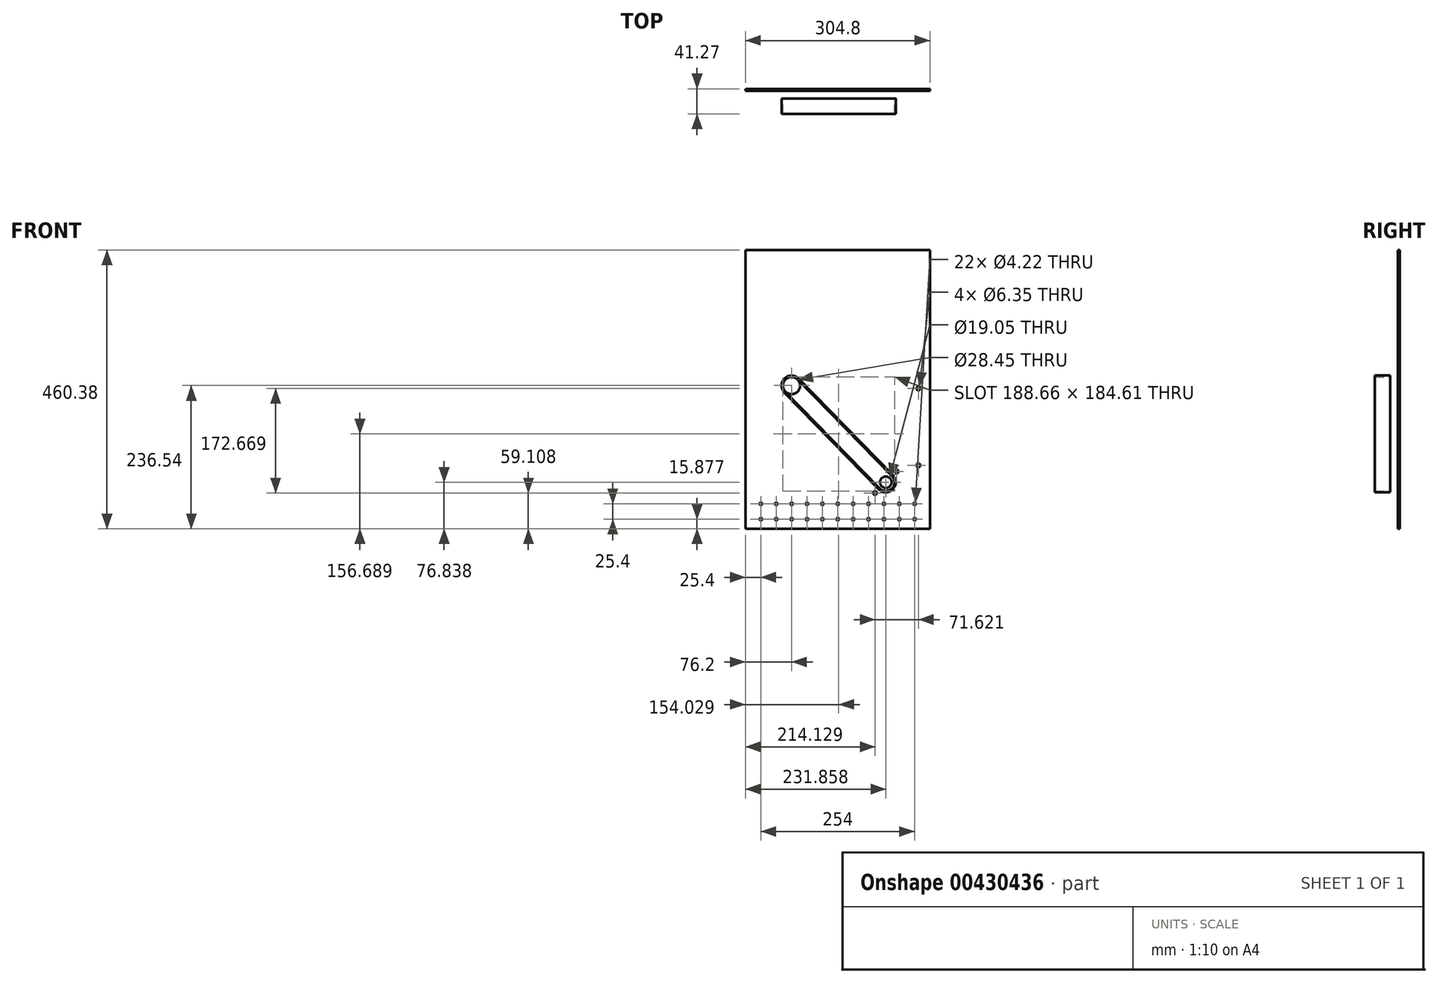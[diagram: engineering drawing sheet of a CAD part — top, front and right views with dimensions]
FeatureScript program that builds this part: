
annotation { "Feature Type Name" : "Feature", "Feature Type Description" : "" }
export const myFeature = defineFeature(function(context is Context, id is Id, definition is map)
    precondition{}
    {
        {
            var Q0;
            Q0=qCreatedBy(makeId("Front.planeOp"),FACE);
            var sketch = newSketch(context, id + "F0", { "sketchPlane" : qUnion([Q0])});
            skCircle(sketch, "E0", {"center": v(0, 0) * mm, "radius": 61.91 * mm, "construction": true});
            skArc(sketch, "E1", {"start": v(0, -182.56) * mm, "mid": v(140.87, -116.12) * mm, "end": v(179.2, 34.83) * mm, "construction": true});
            skLineSegment(sketch, "E2", {"start": v(0, -182.56) * mm, "end": v(132.8, -182.56) * mm, "construction": true});
            skLineSegment(sketch, "E3", {"start": v(228.6, -182.56) * mm, "end": v(228.6, 34.83) * mm, "construction": true});
            skLineSegment(sketch, "E4", {"start": v(228.6, 34.83) * mm, "end": v(179.2, 34.83) * mm, "construction": true});
            skLineSegment(sketch, "E5", {"start": v(0, 0) * mm, "end": v(182.56, 0) * mm, "construction": true});
            skLineSegment(sketch, "E6", {"start": v(0, 0) * mm, "end": v(179.2, 34.83) * mm, "construction": true});
            skLineSegment(sketch, "E7", {"start": v(209.55, -182.56) * mm, "end": v(209.55, 58.37) * mm, "construction": true});
            skCircle(sketch, "E8", {"center": v(209.55, -131.76) * mm, "radius": 3.17 * mm, "construction": true});
            skCircle(sketch, "E9", {"center": v(209.55, -4.76) * mm, "radius": 3.18 * mm, "construction": true});
            skLineSegment(sketch, "E10.top", {"start": v(178.52, -136.84) * mm, "end": v(132.8, -136.84) * mm});
            skLineSegment(sketch, "E10.left", {"start": v(178.52, -182.56) * mm, "end": v(178.52, -136.84) * mm});
            skLineSegment(sketch, "E10.right", {"start": v(132.8, -182.56) * mm, "end": v(132.8, -136.84) * mm});
            skPoint(sketch, "E10.middle", {"position": v(155.66, -159.7) * mm});
            skLineSegment(sketch, "E11.trimOffspring", {"start": v(178.52, -182.56) * mm, "end": v(228.6, -182.56) * mm, "construction": true});
            skSolve(sketch);
        }
        {
            var Q0;
            Q0=qCreatedBy(makeId("Front.planeOp"),FACE);
            var sketch = newSketch(context, id + "F1", { "sketchPlane" : qUnion([Q0])});
            skPoint(sketch, "E12.0", {"position": v(228.6, -182.56) * mm});
            skCircle(sketch, "E13.0", {"center": v(209.55, -131.76) * mm, "radius": 3.17 * mm});
            skCircle(sketch, "E14.0", {"center": v(209.55, -4.76) * mm, "radius": 3.18 * mm});
            skLineSegment(sketch, "E15.top", {"start": v(228.6, 223.84) * mm, "end": v(-76.2, 223.84) * mm});
            skLineSegment(sketch, "E15.left", {"start": v(228.6, -182.56) * mm, "end": v(228.6, 223.84) * mm});
            skLineSegment(sketch, "E15.right", {"start": v(-76.2, -182.56) * mm, "end": v(-76.2, 223.84) * mm});
            skLineSegment(sketch, "E16", {"start": v(228.6, -182.56) * mm, "end": v(-76.2, -182.56) * mm});
            skPoint(sketch, "E17.0", {"position": v(155.66, -159.7) * mm});
            skCircle(sketch, "E18", {"center": v(155.66, -159.7) * mm, "radius": 9.53 * mm});
            skCircle(sketch, "E19", {"center": v(173.39, -141.97) * mm, "radius": 3.18 * mm});
            skCircle(sketch, "E20", {"center": v(137.93, -177.43) * mm, "radius": 3.18 * mm});
            skLineSegment(sketch, "E21.bottom", {"start": v(173.39, -141.97) * mm, "end": v(137.93, -141.97) * mm, "construction": true});
            skLineSegment(sketch, "E21.top", {"start": v(173.39, -177.43) * mm, "end": v(137.93, -177.43) * mm, "construction": true});
            skLineSegment(sketch, "E21.left", {"start": v(173.39, -141.97) * mm, "end": v(173.39, -177.43) * mm, "construction": true});
            skLineSegment(sketch, "E21.right", {"start": v(137.93, -141.97) * mm, "end": v(137.93, -177.43) * mm, "construction": true});
            skCircle(sketch, "E22", {"center": v(0, 0) * mm, "radius": 14.22 * mm});
            skLineSegment(sketch, "E23.bottom", {"start": v(-76.2, -182.56) * mm, "end": v(228.6, -182.56) * mm});
            skLineSegment(sketch, "E23.top", {"start": v(-76.2, -182.56) * mm, "end": v(228.6, -182.56) * mm});
            skLineSegment(sketch, "E23.left", {"start": v(-76.2, -182.56) * mm, "end": v(-76.2, -182.56) * mm});
            skLineSegment(sketch, "E23.right", {"start": v(228.6, -182.56) * mm, "end": v(228.6, -182.56) * mm});
            skLineSegment(sketch, "E24.top", {"start": v(228.6, -236.54) * mm, "end": v(-76.2, -236.54) * mm});
            skLineSegment(sketch, "E24.left", {"start": v(228.6, -182.56) * mm, "end": v(228.6, -236.54) * mm});
            skLineSegment(sketch, "E24.right", {"start": v(-76.2, -182.56) * mm, "end": v(-76.2, -236.54) * mm});
            skCircle(sketch, "E25", {"center": v(-50.8, -195.26) * mm, "radius": 2.1 * mm});
            skCircle(sketch, "E26", {"center": v(-50.8, -220.66) * mm, "radius": 2.1 * mm});
            skCircle(sketch, "E27.1.0.0", {"center": v(-25.4, -195.26) * mm, "radius": 2.1 * mm});
            skCircle(sketch, "E27.1.0.1", {"center": v(-25.4, -220.66) * mm, "radius": 2.1 * mm});
            skCircle(sketch, "E27.2.0.0", {"center": v(0, -195.26) * mm, "radius": 2.1 * mm});
            skCircle(sketch, "E27.2.0.1", {"center": v(0, -220.66) * mm, "radius": 2.1 * mm});
            skCircle(sketch, "E27.3.0.0", {"center": v(25.4, -195.26) * mm, "radius": 2.1 * mm});
            skCircle(sketch, "E27.3.0.1", {"center": v(25.4, -220.66) * mm, "radius": 2.1 * mm});
            skCircle(sketch, "E27.4.0.0", {"center": v(50.8, -195.26) * mm, "radius": 2.1 * mm});
            skCircle(sketch, "E27.4.0.1", {"center": v(50.8, -220.66) * mm, "radius": 2.1 * mm});
            skCircle(sketch, "E27.5.0.0", {"center": v(76.2, -195.26) * mm, "radius": 2.1 * mm});
            skCircle(sketch, "E27.5.0.1", {"center": v(76.2, -220.66) * mm, "radius": 2.1 * mm});
            skCircle(sketch, "E27.6.0.0", {"center": v(101.6, -195.26) * mm, "radius": 2.1 * mm});
            skCircle(sketch, "E27.6.0.1", {"center": v(101.6, -220.66) * mm, "radius": 2.1 * mm});
            skCircle(sketch, "E27.7.0.0", {"center": v(127, -195.26) * mm, "radius": 2.1 * mm});
            skCircle(sketch, "E27.7.0.1", {"center": v(127, -220.66) * mm, "radius": 2.1 * mm});
            skCircle(sketch, "E27.8.0.0", {"center": v(152.4, -195.26) * mm, "radius": 2.1 * mm});
            skCircle(sketch, "E27.8.0.1", {"center": v(152.4, -220.66) * mm, "radius": 2.1 * mm});
            skCircle(sketch, "E27.9.0.0", {"center": v(177.8, -195.26) * mm, "radius": 2.1 * mm});
            skCircle(sketch, "E27.9.0.1", {"center": v(177.8, -220.66) * mm, "radius": 2.1 * mm});
            skCircle(sketch, "E27.10.0.0", {"center": v(203.2, -195.26) * mm, "radius": 2.1 * mm});
            skCircle(sketch, "E27.10.0.1", {"center": v(203.2, -220.66) * mm, "radius": 2.1 * mm});
            skCircle(sketch, "E27.11.0.0", {"center": v(228.6, -195.26) * mm, "radius": 2.1 * mm, "construction": true});
            skCircle(sketch, "E27.11.0.1", {"center": v(228.6, -220.66) * mm, "radius": 2.1 * mm, "construction": true});
            skCircle(sketch, "E27.12.0.0", {"center": v(254, -195.26) * mm, "radius": 2.1 * mm, "construction": true});
            skCircle(sketch, "E27.12.0.1", {"center": v(254, -220.66) * mm, "radius": 2.1 * mm, "construction": true});
            skCircle(sketch, "E27.13.0.0", {"center": v(279.4, -195.26) * mm, "radius": 2.1 * mm, "construction": true});
            skCircle(sketch, "E27.13.0.1", {"center": v(279.4, -220.66) * mm, "radius": 2.1 * mm, "construction": true});
            skCircle(sketch, "E27.14.0.0", {"center": v(304.8, -195.26) * mm, "radius": 2.1 * mm, "construction": true});
            skCircle(sketch, "E27.14.0.1", {"center": v(304.8, -220.66) * mm, "radius": 2.1 * mm, "construction": true});
            skLineSegment(sketch, "E27.direction1", {"start": v(-50.8, -195.26) * mm, "end": v(-25.4, -195.26) * mm, "construction": true});
            skSolve(sketch);
        }
        {
            var Q0;
            Q0=makeQuery(id+"F1.imprint","IMPRINT",FACE,{"disambiguationData":[TD([[makeQuery(id+"F1.imprint","IMPRINT",EDGE,{"derivedFrom":sQuery(id+"F1.wireOp",EDGE,"E13.0")}),-1.0]])]});
            var Q1;
            Q1=makeQuery(id+"F1.imprint","IMPRINT",FACE,{"disambiguationData":[TD([[makeQuery(id+"F1.imprint","IMPRINT",EDGE,{"derivedFrom":sQuery(id+"F1.wireOp",EDGE,"E16")}),1.0]])]});
            extrude(context, id + "F2", {"entities" : qUnion([Q0, Q1]), "depth" : 3.17 * mm, "offsetDistance" : 25.4 * mm});
        }
        {
            var Q0;
            Q0=makeQuery(id+"F2.opExtrude","CAP_FACE",FACE,{"disambiguationData":[OSD([sQuery(id+"F1.wireOp",EDGE,"E13.0"),sQuery(id+"F1.wireOp",EDGE,"E14.0"),sQuery(id+"F1.wireOp",EDGE,"E15.top"),sQuery(id+"F1.wireOp",EDGE,"E15.left"),sQuery(id+"F1.wireOp",EDGE,"E15.right"),sQuery(id+"F1.wireOp",EDGE,"E16"),sQuery(id+"F1.wireOp",EDGE,"E18"),sQuery(id+"F1.wireOp",EDGE,"E19"),sQuery(id+"F1.wireOp",EDGE,"E20"),sQuery(id+"F1.wireOp",EDGE,"E22")])],"isStart":false});
            cPlane(context, id + "F3", {"entities" : qUnion([Q0]), "cplaneType" : CPlaneType.OFFSET, "offset" : 12.7 * mm, "width" : 152.4 * mm, "height" : 152.4 * mm});
        }
        {
            var Q0;
            Q0=qCreatedBy(id+"F3.planeOp",FACE);
            var sketch = newSketch(context, id + "F4", { "sketchPlane" : qUnion([Q0])});
            skCircle(sketch, "E28.0", {"center": v(155.66, -159.7) * mm, "radius": 9.53 * mm});
            skCircle(sketch, "E29.0", {"center": v(0, 0) * mm, "radius": 14.22 * mm});
            skArc(sketch, "E30", {"start": v(143.84, -171.23) * mm, "mid": v(167.18, -171.53) * mm, "end": v(167.48, -148.18) * mm});
            skArc(sketch, "E31", {"start": v(11.82, 11.52) * mm, "mid": v(-11.52, 11.82) * mm, "end": v(-11.82, -11.52) * mm});
            skLineSegment(sketch, "E32", {"start": v(167.48, -148.18) * mm, "end": v(11.82, 11.52) * mm});
            skLineSegment(sketch, "E33", {"start": v(-11.82, -11.52) * mm, "end": v(143.84, -171.23) * mm});
            skLineSegment(sketch, "E34.0", {"start": v(166.03, -149.6) * mm, "end": v(10.37, 10.1) * mm});
            skArc(sketch, "E34.1", {"start": v(145.3, -169.8) * mm, "mid": v(165.76, -170.07) * mm, "end": v(166.03, -149.6) * mm});
            skLineSegment(sketch, "E34.2", {"start": v(-10.37, -10.1) * mm, "end": v(145.3, -169.8) * mm});
            skArc(sketch, "E34.3", {"start": v(10.37, 10.1) * mm, "mid": v(-10.1, 10.37) * mm, "end": v(-10.37, -10.1) * mm});
            skSolve(sketch);
        }
        {
            var Q0;
            Q0=makeQuery(id+"F4.imprint","IMPRINT",FACE,{"disambiguationData":[TD([[makeQuery(id+"F4.imprint","IMPRINT",EDGE,{"derivedFrom":sQuery(id+"F4.wireOp",EDGE,"E30")}),1.0]])]});
            extrude(context, id + "F5", {"entities" : qUnion([Q0]), "depth" : 25.4 * mm, "offsetDistance" : 25.4 * mm});
        }
    });
